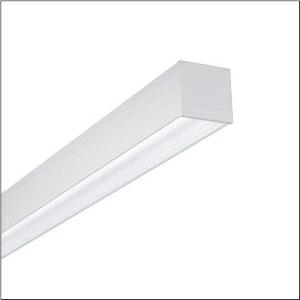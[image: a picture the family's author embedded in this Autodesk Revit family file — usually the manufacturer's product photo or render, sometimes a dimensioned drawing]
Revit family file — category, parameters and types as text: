
# Revit family: silica_r_5mx21bd1e4a_4ae4
name_source: partatom
category: Lighting Fixtures
units: mm (PartAtom-declared; Revit-internal decimal feet)

## family parameters
Cut with Voids When Loaded = No
Host = Face
Light Source = No
Part Type = Normal
Room Calculation Point = No
Round Connector Dimension = Use Diameter
Shared = No

## types (1)
- --- (1 x LED, 4950 lm, 29.3 W, 4000K)
    Apparent Load = 29 VA
    CIE Flux Codes = 82 97 100 100 100
    Color Rendering = 80
    Color Temperature = 4000K
    Default Elevation = 1800 mm
    Description = Silica®, office luminaire, of aluminium, light emission: direct distribution, primary light characteristic: symmetric, installation type: surface-mounted, LED rated luminous flux: 4.950 lm, light colour: 840, colour temperature: 4000K, control gear: ECG DALI, with terminal, 3+2-pole, max. 2.5mm², mains connection: 230V, AC, 50/60Hz, rated input power: 29W, luminaire housing, of aluminium, anodised, silver, length: 1.440 mm, width: 64 mm, height: 64mm, protection rating (complete): IP20, insulation class (complete): insulation class I (protective earthing), certification: CE, permissible ambient temperature for indoor applications: 0..+35°C, standard: EN 50419, packaging unit: 1 piece
    Height = 64 mm
    Lamp = 1 x LED
    Lamp Light Flux = 4950 lm
    Lamp Power = 29.3 W
    Lamp count = 1
    Length = 1442 mm
    Luminous efficacy = 169 lm/W
    Manufacturer = Siteco
    ModVariant = No
    Model = 5MX21BD1E4A
    Mounting Place = Ceiling
    Mounting Type = Surface mounted
    Number of Poles = 1
    OnlyDefault = Yes
    Power Factor = 1
    Product Name = Silica®
    Product group = office luminaire | ceiling mounted
    ProductGroupID = 302
    Protection Class = Protection class I
    Protection Degree = IP 20
    RLX_Detail_Level = 1
    RlxData = <blob elided: 27265 chars, md5=855c57d4>
    Socket = socket
    Standby Power = 0 W
    System Light Flux = 4950 lm
    System Power = 29 W
    Type Comments = factory setting: luminous flux: 100 % | dim-lin: 254 | 163 mA
    Type Image = l_1004827.jpg
    URL = http://relux.com
    VarID = @adj_132232
    Voltage = 0 V
    Weight = 0.00 kg
    Width = 66 mm

## geometry (parser evidence)
native form markers: Blend x4, Sweep x9
no freeform markers — native parametric forms only
